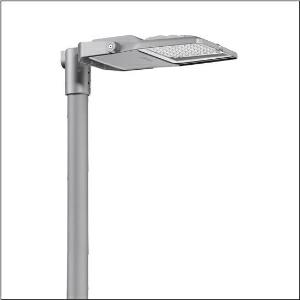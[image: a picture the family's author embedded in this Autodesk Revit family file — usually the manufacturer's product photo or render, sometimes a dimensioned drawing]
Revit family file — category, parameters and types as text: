
# Revit family: floodlight_fl_21_iq_mini___pl33t_5xa7772d4f3a_7ca2
name_source: partatom
category: Lighting Fixtures
units: mm (PartAtom-declared; Revit-internal decimal feet)

## family parameters
Cut with Voids When Loaded = No
Host = Face
Light Source = No
Part Type = Normal
Room Calculation Point = No
Round Connector Dimension = Use Diameter
Shared = No

## types (1)
- --- (1 x LED, 18390 lm, 143 W, 4000K)
    Apparent Load = 143 VA
    CIE Flux Codes = 26 75 99 100 100
    Color Rendering = 70
    Color Temperature = 4000K
    Default Elevation = 1800 mm
    Description = Floodlight FL 21 iQ mini, floodlight, primary light control with lens, of PMMA, primary optical cover: protective disc, of toughened safety glass, transparent, light distribution: PL33T, light emission: direct distribution, installation type: surface-mounted, LED, High Power LED, rated luminous flux: 18.390lm, luminous efficacy: 129lm/W, light colour: 740, colour temperature: 4000K, control: Auto-Match, Temp-Guard, Night-Set, Smart-Wire, Desk-Remote (wireless, voltage-free reading and setting of iQ features in the workshop via application-optimized NFC function/RFID function), optimised constant luminous flux control (CLO 2.0), Light-Fading, Lumen-Switch, with terminal, 6-pole, mains connection: 220..240V, AC, 50/60Hz, start of lifetime: 143W, end of service life: 152W, reduction: 61W, luminaire housing, of diecast aluminium, powder-coated, Siteco® metallic grey (DB 702S), corrosivity category C5 mid according to DIN EN ISO 12944, sealing non-destructively replaceable, please order mast flange separately, mast bracket, of steel, galvanised, powder-coated, protection rating (complete): IP66, insulation class (complete): insulation class II (safety insulation), certification: CE, ENEC, VDE, protection symbol: D, impact resistance: IK08, permissible operating ambient temperature: -40..+40°C, permissible operating ambient temperature for outdoor applications: -40..+50°C, standard: DIN EN 12944, LABS conformity tested according to VDMA 24364:2018-05, packaging unit: 1 piece

Light Distribution: PL33T
    Height = 70 mm
    Lamp = 1 x LED
    Lamp Light Flux = 18390 lm
    Lamp Power = 143 W
    Lamp count = 1
    Length = 485 mm
    Luminous efficacy = 129 lm/W
    Manufacturer = Siteco
    ModVariant = No
    Model = 5XA7772D4F3A
    Number of Poles = 1
    OnlyDefault = Yes
    Power Factor = 1
    Product Name = Floodlight FL 21 iQ mini | PL33T
    Product group = floodlight | pylon annexe
    ProductGroupID = 6200
    Protection Class = Protection class II
    Protection Degree = IP 66
    RLX_Detail_Level = 1
    RLX_Emergency_Light_Flux = 0 lm
    RLX_Emergency_Type = 0
    RLX_Emergency_Type_DB = No
    RlxData = <blob elided: 102585 chars, md5=a167bf6c>
    Socket = socket
    Standby Power = 0 W
    System Light Flux = 18390 lm
    System Power = 143 W
    Type Comments = factory setting: luminous flux: 100 % | dim-lin: 254 | 730 mA
    Type Image = l_1007125.jpg
    URL = http://relux.com
    VarID = @adj_081263
    Voltage = 0 V
    Weight = 0.00 kg
    Width = 337 mm

## geometry (parser evidence)
native form markers: Blend x4, Sweep x13
no freeform markers — native parametric forms only
